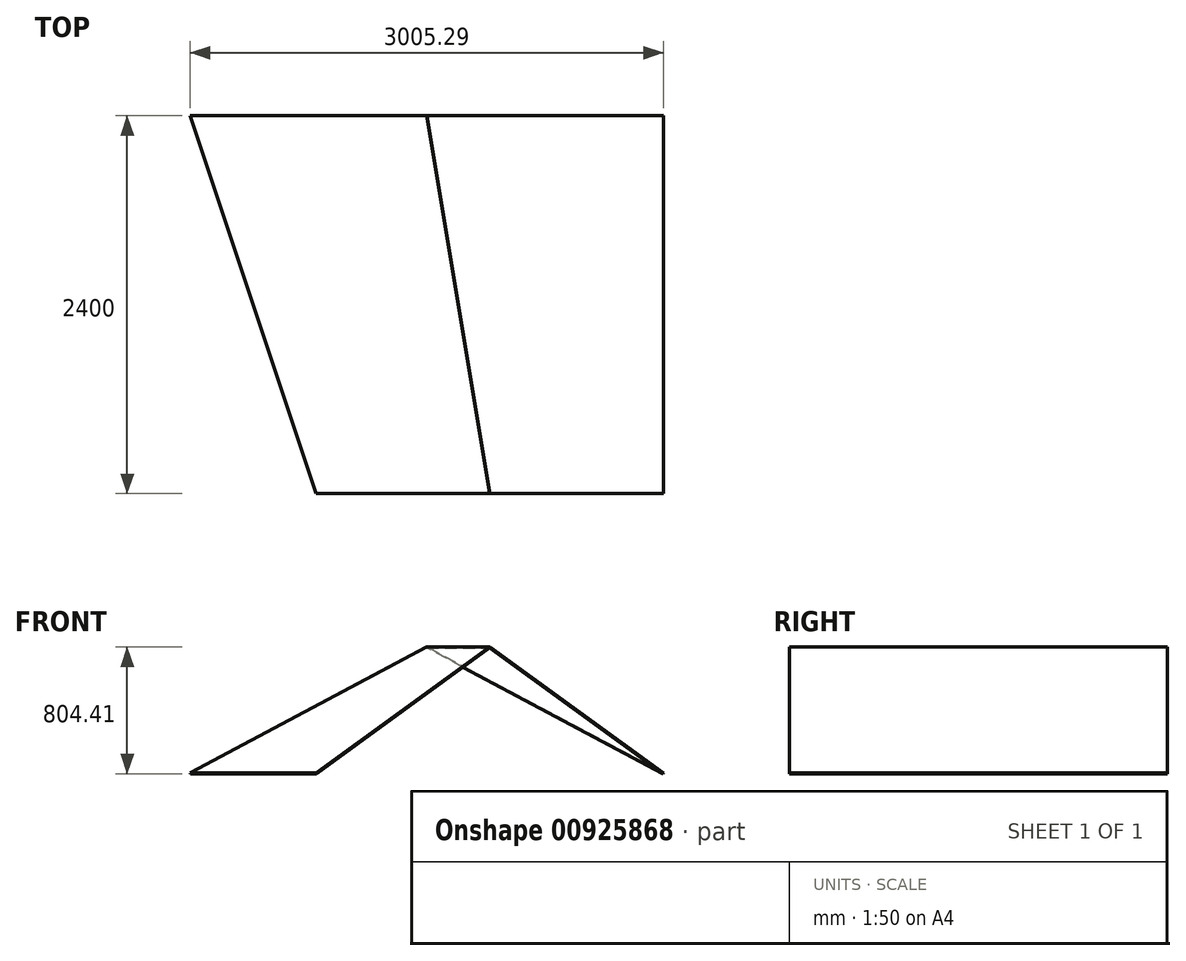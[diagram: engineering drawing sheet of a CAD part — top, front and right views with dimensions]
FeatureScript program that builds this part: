
annotation { "Feature Type Name" : "Feature", "Feature Type Description" : "" }
export const myFeature = defineFeature(function(context is Context, id is Id, definition is map)
    precondition{}
    {
        {
            var Q0;
            Q0=qCreatedBy(makeId("Front.planeOp"),FACE);
            var sketch = newSketch(context, id + "F0", { "sketchPlane" : qUnion([Q0])});
            skLineSegment(sketch, "E0", {"start": v(-1500, 0) * mm, "end": v(1500, 0) * mm});
            skLineSegment(sketch, "E1", {"start": v(1500, 0) * mm, "end": v(0, 800) * mm});
            skLineSegment(sketch, "E2", {"start": v(0, 800) * mm, "end": v(-1500, 0) * mm});
            skLineSegment(sketch, "E3", {"start": v(0, 0) * mm, "end": v(0, 1174.89) * mm, "construction": true});
            skSolve(sketch);
        }
        {
            var Q0;
            Q0=qCreatedBy(makeId("Front.planeOp"),FACE);
            cPlane(context, id + "F1", {"entities" : qUnion([Q0]), "cplaneType" : CPlaneType.OFFSET, "offset" : 2400 * mm, "width" : 150 * mm, "height" : 150 * mm});
        }
        {
            var Q0;
            Q0=qCreatedBy(id+"F1.planeOp",FACE);
            var sketch = newSketch(context, id + "F2", { "sketchPlane" : qUnion([Q0])});
            skLineSegment(sketch, "E4", {"start": v(1500, 0) * mm, "end": v(400, 800) * mm});
            skLineSegment(sketch, "E5", {"start": v(400, 800) * mm, "end": v(-700, 0) * mm});
            skLineSegment(sketch, "E6", {"start": v(-700, 0) * mm, "end": v(1500, 0) * mm});
            skLineSegment(sketch, "E7", {"start": v(400, 0) * mm, "end": v(400, 800) * mm, "construction": true});
            skSolve(sketch);
        }
        {
            var Q0;
            Q0=makeQuery(id+"F0.imprint","IMPRINT",FACE,{"disambiguationData":[TD([[makeQuery(id+"F0.imprint","IMPRINT",EDGE,{"derivedFrom":sQuery(id+"F0.wireOp",EDGE,"E0")}),1.0]])]});
            var sketch = newSketch(context, id + "F3", { "sketchPlane" : qUnion([Q0])});
            skLineSegment(sketch, "E8.0", {"start": v(1500, 0) * mm, "end": v(0, 800) * mm});
            skLineSegment(sketch, "E9.0", {"start": v(1502.35, 4.41) * mm, "end": v(2.35, 804.41) * mm});
            skLineSegment(sketch, "E10", {"start": v(0, 800) * mm, "end": v(2.35, 804.41) * mm});
            skLineSegment(sketch, "E11", {"start": v(1500, 0) * mm, "end": v(1502.35, 4.41) * mm});
            skSolve(sketch);
        }
        {
            var Q0;
            Q0=makeQuery(id+"F2.imprint","IMPRINT",FACE,{"disambiguationData":[TD([[makeQuery(id+"F2.imprint","IMPRINT",EDGE,{"derivedFrom":sQuery(id+"F2.wireOp",EDGE,"E4")}),1.0]])]});
            var sketch = newSketch(context, id + "F4", { "sketchPlane" : qUnion([Q0])});
            skLineSegment(sketch, "E12.0", {"start": v(1500, 0) * mm, "end": v(400, 800) * mm});
            skLineSegment(sketch, "E13.0", {"start": v(1502.94, 4.04) * mm, "end": v(402.94, 804.04) * mm});
            skLineSegment(sketch, "E14", {"start": v(400, 800) * mm, "end": v(402.94, 804.04) * mm});
            skLineSegment(sketch, "E15", {"start": v(1500, 0) * mm, "end": v(1502.94, 4.04) * mm});
            skSolve(sketch);
        }
        {
            var Q0;
            Q0=makeQuery(id+"F3.imprint","IMPRINT",FACE,{"disambiguationData":[TD([[makeQuery(id+"F3.imprint","IMPRINT",EDGE,{"derivedFrom":sQuery(id+"F3.wireOp",EDGE,"E8.0")}),-1.0]])]});
            var Q1;
            Q1=makeQuery(id+"F4.imprint","IMPRINT",FACE,{"disambiguationData":[TD([[makeQuery(id+"F4.imprint","IMPRINT",EDGE,{"derivedFrom":sQuery(id+"F4.wireOp",EDGE,"E12.0")}),-1.0]])]});
            loft(context, id + "F5", {"sheetProfilesArray" : [{ "sheetProfileEntities" : qUnion([Q0]) }, { "sheetProfileEntities" : qUnion([Q1]) }]});
        }
        {
            var Q0;
            Q0=makeQuery(id+"F0.imprint","IMPRINT",FACE,{"disambiguationData":[TD([[makeQuery(id+"F0.imprint","IMPRINT",EDGE,{"derivedFrom":sQuery(id+"F0.wireOp",EDGE,"E0")}),1.0]])]});
            var sketch = newSketch(context, id + "F6", { "sketchPlane" : qUnion([Q0])});
            skLineSegment(sketch, "E16.0", {"start": v(0, 800) * mm, "end": v(-1500, 0) * mm});
            skLineSegment(sketch, "E17.0", {"start": v(-2.35, 804.41) * mm, "end": v(-1502.35, 4.41) * mm});
            skLineSegment(sketch, "E18", {"start": v(0, 800) * mm, "end": v(-2.35, 804.41) * mm});
            skLineSegment(sketch, "E19", {"start": v(-1500, 0) * mm, "end": v(-1502.35, 4.41) * mm});
            skSolve(sketch);
        }
        {
            var Q0;
            Q0=makeQuery(id+"F2.imprint","IMPRINT",FACE,{"disambiguationData":[TD([[makeQuery(id+"F2.imprint","IMPRINT",EDGE,{"derivedFrom":sQuery(id+"F2.wireOp",EDGE,"E4")}),1.0]])]});
            var sketch = newSketch(context, id + "F7", { "sketchPlane" : qUnion([Q0])});
            skLineSegment(sketch, "E20.0", {"start": v(400, 800) * mm, "end": v(-700, 0) * mm});
            skLineSegment(sketch, "E21.0", {"start": v(397.06, 804.04) * mm, "end": v(-702.94, 4.04) * mm});
            skLineSegment(sketch, "E22", {"start": v(400, 800) * mm, "end": v(397.06, 804.04) * mm});
            skLineSegment(sketch, "E23", {"start": v(-700, 0) * mm, "end": v(-702.94, 4.04) * mm});
            skSolve(sketch);
        }
        {
            var Q0;
            Q0=makeQuery(id+"F6.imprint","IMPRINT",FACE,{"disambiguationData":[TD([[makeQuery(id+"F6.imprint","IMPRINT",EDGE,{"derivedFrom":sQuery(id+"F6.wireOp",EDGE,"E16.0")}),-1.0]])]});
            var Q1;
            Q1=makeQuery(id+"F7.imprint","IMPRINT",FACE,{"disambiguationData":[TD([[makeQuery(id+"F7.imprint","IMPRINT",EDGE,{"derivedFrom":sQuery(id+"F7.wireOp",EDGE,"E20.0")}),-1.0]])]});
            loft(context, id + "F8", {"sheetProfilesArray" : [{ "sheetProfileEntities" : qUnion([Q0]) }, { "sheetProfileEntities" : qUnion([Q1]) }]});
        }
    });
